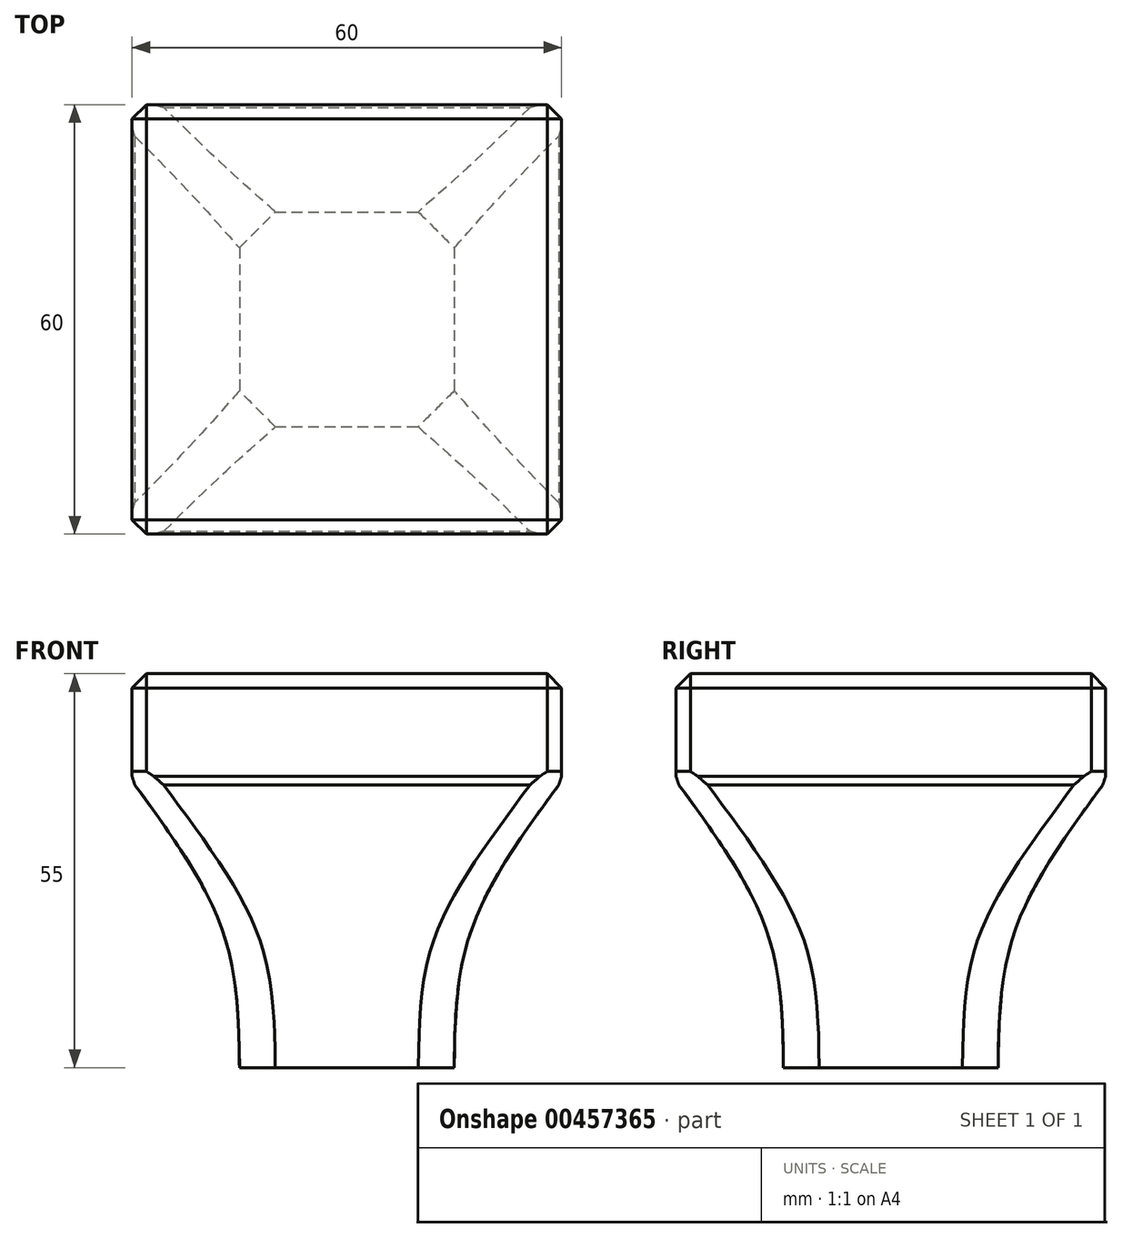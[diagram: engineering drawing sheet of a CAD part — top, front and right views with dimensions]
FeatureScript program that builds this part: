
annotation { "Feature Type Name" : "Feature", "Feature Type Description" : "" }
export const myFeature = defineFeature(function(context is Context, id is Id, definition is map)
    precondition{}
    {
        {
            var Q0;
            Q0=qCreatedBy(makeId("Top.planeOp"),FACE);
            var sketch = newSketch(context, id + "F0", { "sketchPlane" : qUnion([Q0])});
            skLineSegment(sketch, "E0.bottom", {"start": v(30, 30) * mm, "end": v(-30, 30) * mm});
            skLineSegment(sketch, "E0.top", {"start": v(30, -30) * mm, "end": v(-30, -30) * mm});
            skLineSegment(sketch, "E0.left", {"start": v(30, 30) * mm, "end": v(30, -30) * mm});
            skLineSegment(sketch, "E0.right", {"start": v(-30, 30) * mm, "end": v(-30, -30) * mm});
            skPoint(sketch, "E0.middle", {"position": v(0, 0) * mm});
            skSolve(sketch);
        }
        {
            var Q0;
            Q0 = qSketchRegion(id + "F0", true);
            extrude(context, id + "F1", {"entities" : qUnion([Q0]), "depth" : 40 * mm});
        }
        {
            var Q0;
            Q0=makeQuery(id+"F1.opExtrude","SWEPT_FACE",FACE,{"disambiguationData":[OSD([sQuery(id+"F0.wireOp",EDGE,"E0.top")])]});
            var sketch = newSketch(context, id + "F2", { "sketchPlane" : qUnion([Q0])});
            skLineSegment(sketch, "E1", {"start": v(-30, 0) * mm, "end": v(-15, 0) * mm});
            skLineSegment(sketch, "E2", {"start": v(30, 0) * mm, "end": v(15, 0) * mm});
            skLineSegment(sketch, "E3", {"start": v(-30, 40) * mm, "end": v(-30, 0) * mm});
            skLineSegment(sketch, "E4", {"start": v(30, 0) * mm, "end": v(30, 40) * mm});
            skFitSpline(sketch, "E5", {"points": [v(-15, 0) * mm, v(-17.35, 19.1) * mm, v(-30, 40) * mm], "startDerivative": vector(-0.56, 40.9) * mm, "endDerivative": vector(-28.87, 39.13) * mm});
            skFitSpline(sketch, "E6.MirrorCS", {"points": [v(15, 0) * mm, v(17.35, 19.1) * mm, v(30, 40) * mm], "startDerivative": vector(0.56, 40.9) * mm, "endDerivative": vector(28.87, 39.13) * mm});
            skSolve(sketch);
        }
        {
            var Q0;
            Q0=makeQuery(id+"F1.opExtrude","SWEPT_FACE",FACE,{"disambiguationData":[OSD([sQuery(id+"F0.wireOp",EDGE,"E0.left")])]});
            var sketch = newSketch(context, id + "F3", { "sketchPlane" : qUnion([Q0])});
            skLineSegment(sketch, "E7", {"start": v(-30, 0) * mm, "end": v(-15, 0) * mm});
            skLineSegment(sketch, "E8", {"start": v(30, 0) * mm, "end": v(15, 0) * mm});
            skLineSegment(sketch, "E9", {"start": v(-30, 40) * mm, "end": v(-30, 0) * mm});
            skLineSegment(sketch, "E10", {"start": v(30, 0) * mm, "end": v(30, 40) * mm});
            skFitSpline(sketch, "E11", {"points": [v(-15, 0) * mm, v(-17.35, 19.1) * mm, v(-30, 40) * mm], "startDerivative": vector(-0.56, 40.9) * mm, "endDerivative": vector(-28.87, 39.13) * mm});
            skFitSpline(sketch, "E12.MirrorCS", {"points": [v(15, 0) * mm, v(17.35, 19.1) * mm, v(30, 40) * mm], "startDerivative": vector(0.56, 40.9) * mm, "endDerivative": vector(28.87, 39.13) * mm});
            skSolve(sketch);
        }
        {
            var Q0;
            Q0 = qSketchRegion(id + "F2", true);
            extrude(context, id + "F4", {"entities" : qUnion([Q0]), "operationType" : NewBodyOperationType.REMOVE, "oppositeDirection" : true, "depth" : 60 * mm});
        }
        {
            var Q0;
            Q0 = qSketchRegion(id + "F3", true);
            extrude(context, id + "F5", {"entities" : qUnion([Q0]), "operationType" : NewBodyOperationType.REMOVE, "oppositeDirection" : true, "depth" : 60 * mm});
        }
        {
            var Q0;
            Q0=makeQuery(id+"F1.opExtrude","CAP_FACE",FACE,{"disambiguationData":[OSD([sQuery(id+"F0.wireOp",EDGE,"E0.bottom"),sQuery(id+"F0.wireOp",EDGE,"E0.top"),sQuery(id+"F0.wireOp",EDGE,"E0.left"),sQuery(id+"F0.wireOp",EDGE,"E0.right")])],"isStart":false});
            var sketch = newSketch(context, id + "F6", { "sketchPlane" : qUnion([Q0])});
            skLineSegment(sketch, "E13.bottom", {"start": v(30, 30) * mm, "end": v(-30, 30) * mm});
            skLineSegment(sketch, "E13.top", {"start": v(30, -30) * mm, "end": v(-30, -30) * mm});
            skLineSegment(sketch, "E13.left", {"start": v(30, 30) * mm, "end": v(30, -30) * mm});
            skLineSegment(sketch, "E13.right", {"start": v(-30, 30) * mm, "end": v(-30, -30) * mm});
            skPoint(sketch, "E13.middle", {"position": v(0, 0) * mm});
            skSolve(sketch);
        }
        {
            var Q0;
            Q0 = qSketchRegion(id + "F6", true);
            extrude(context, id + "F7", {"entities" : qUnion([Q0]), "operationType" : NewBodyOperationType.ADD, "depth" : 15 * mm});
        }
        {
            var Q0;
            Q0=makeQuery(id+"F5.boolean.opBoolean","INTERSECT",EDGE,{"derivedFrom":[makeQuery(id+"F4.boolean.opBoolean","COPY",FACE,{"derivedFrom":makeQuery(id+"F4.opExtrude","SWEPT_FACE",FACE,{"disambiguationData":[OSD([sQuery(id+"F2.wireOp",EDGE,"E5")])]})}),makeQuery(id+"F5.opExtrude","SWEPT_FACE",FACE,{"disambiguationData":[OSD([sQuery(id+"F3.wireOp",EDGE,"E11")])]})]});
            var Q1;
            Q1=makeQuery(id+"F5.boolean.opBoolean","INTERSECT",EDGE,{"derivedFrom":[makeQuery(id+"F4.boolean.opBoolean","COPY",FACE,{"derivedFrom":makeQuery(id+"F4.opExtrude","SWEPT_FACE",FACE,{"disambiguationData":[OSD([sQuery(id+"F2.wireOp",EDGE,"E6.MirrorCS")])]})}),makeQuery(id+"F5.opExtrude","SWEPT_FACE",FACE,{"disambiguationData":[OSD([sQuery(id+"F3.wireOp",EDGE,"E11")])]})]});
            var Q2;
            Q2=makeQuery(id+"F5.boolean.opBoolean","INTERSECT",EDGE,{"derivedFrom":[makeQuery(id+"F4.boolean.opBoolean","COPY",FACE,{"derivedFrom":makeQuery(id+"F4.opExtrude","SWEPT_FACE",FACE,{"disambiguationData":[OSD([sQuery(id+"F2.wireOp",EDGE,"E6.MirrorCS")])]})}),makeQuery(id+"F5.opExtrude","SWEPT_FACE",FACE,{"disambiguationData":[OSD([sQuery(id+"F3.wireOp",EDGE,"E12.MirrorCS")])]})]});
            var Q3;
            Q3=makeQuery(id+"F5.boolean.opBoolean","INTERSECT",EDGE,{"derivedFrom":[makeQuery(id+"F4.boolean.opBoolean","COPY",FACE,{"derivedFrom":makeQuery(id+"F4.opExtrude","SWEPT_FACE",FACE,{"disambiguationData":[OSD([sQuery(id+"F2.wireOp",EDGE,"E5")])]})}),makeQuery(id+"F5.opExtrude","SWEPT_FACE",FACE,{"disambiguationData":[OSD([sQuery(id+"F3.wireOp",EDGE,"E12.MirrorCS")])]})]});
            chamfer(context, id + "F8", {"entities" : qUnion([Q0, Q1, Q2, Q3]), "width" : 5 * mm, "tangentPropagation" : true});
        }
        {
            var Q0;
            Q0=makeQuery(id+"F7.opExtrude","SWEPT_EDGE",EDGE,{"disambiguationData":[OSD([sQuery(id+"F6.wireOp",EDGE,"E13.top"),sQuery(id+"F6.wireOp",EDGE,"E13.left")])]});
            var Q1;
            Q1=makeQuery(id+"F7.opExtrude","SWEPT_EDGE",EDGE,{"disambiguationData":[OSD([sQuery(id+"F6.wireOp",EDGE,"E13.bottom"),sQuery(id+"F6.wireOp",EDGE,"E13.left")])]});
            var Q2;
            Q2=makeQuery(id+"F7.boolean.opBoolean","MERGE",EDGE,{"derivedFrom":[makeQuery(id+"F4.boolean.opBoolean","MERGE",EDGE,{"derivedFrom":[makeQuery(id+"F1.opExtrude","CAP_EDGE",EDGE,{"disambiguationData":[OSD([sQuery(id+"F0.wireOp",EDGE,"E0.left")])],"isStart":false}),makeQuery(id+"F4.opExtrude","SWEPT_EDGE",EDGE,{"disambiguationData":[OSD([sQuery(id+"F0.wireOp",EDGE,"E0.top"),sQuery(id+"F2.wireOp",EDGE,"E4"),sQuery(id+"F2.wireOp",EDGE,"E6.MirrorCS")])]})]}),makeQuery(id+"F7.opExtrude","CAP_EDGE",EDGE,{"disambiguationData":[OSD([sQuery(id+"F6.wireOp",EDGE,"E13.left")])],"isStart":true})]});
            var Q3;
            Q3=makeQuery(id+"F7.boolean.opBoolean","MERGE",EDGE,{"derivedFrom":[makeQuery(id+"F5.boolean.opBoolean","MERGE",EDGE,{"derivedFrom":[makeQuery(id+"F1.opExtrude","CAP_EDGE",EDGE,{"disambiguationData":[OSD([sQuery(id+"F0.wireOp",EDGE,"E0.bottom")])],"isStart":false}),makeQuery(id+"F5.opExtrude","SWEPT_EDGE",EDGE,{"disambiguationData":[OSD([sQuery(id+"F0.wireOp",EDGE,"E0.left"),sQuery(id+"F3.wireOp",EDGE,"E10"),sQuery(id+"F3.wireOp",EDGE,"E12.MirrorCS")])]})]}),makeQuery(id+"F7.opExtrude","CAP_EDGE",EDGE,{"disambiguationData":[OSD([sQuery(id+"F6.wireOp",EDGE,"E13.bottom")])],"isStart":true})]});
            var Q4;
            Q4=makeQuery(id+"F7.opExtrude","SWEPT_EDGE",EDGE,{"disambiguationData":[OSD([sQuery(id+"F6.wireOp",EDGE,"E13.bottom"),sQuery(id+"F6.wireOp",EDGE,"E13.right")])]});
            var Q5;
            Q5=makeQuery(id+"F7.boolean.opBoolean","MERGE",EDGE,{"derivedFrom":[makeQuery(id+"F4.boolean.opBoolean","MERGE",EDGE,{"derivedFrom":[makeQuery(id+"F1.opExtrude","CAP_EDGE",EDGE,{"disambiguationData":[OSD([sQuery(id+"F0.wireOp",EDGE,"E0.right")])],"isStart":false}),makeQuery(id+"F4.opExtrude","SWEPT_EDGE",EDGE,{"disambiguationData":[OSD([sQuery(id+"F0.wireOp",EDGE,"E0.top"),sQuery(id+"F2.wireOp",EDGE,"E3"),sQuery(id+"F2.wireOp",EDGE,"E5")])]})]}),makeQuery(id+"F7.opExtrude","CAP_EDGE",EDGE,{"disambiguationData":[OSD([sQuery(id+"F6.wireOp",EDGE,"E13.right")])],"isStart":true})]});
            var Q6;
            Q6=makeQuery(id+"F7.opExtrude","SWEPT_EDGE",EDGE,{"disambiguationData":[OSD([sQuery(id+"F6.wireOp",EDGE,"E13.top"),sQuery(id+"F6.wireOp",EDGE,"E13.right")])]});
            var Q7;
            Q7=makeQuery(id+"F7.boolean.opBoolean","MERGE",EDGE,{"derivedFrom":[makeQuery(id+"F5.boolean.opBoolean","MERGE",EDGE,{"derivedFrom":[makeQuery(id+"F1.opExtrude","CAP_EDGE",EDGE,{"disambiguationData":[OSD([sQuery(id+"F0.wireOp",EDGE,"E0.top")])],"isStart":false}),makeQuery(id+"F5.opExtrude","SWEPT_EDGE",EDGE,{"disambiguationData":[OSD([sQuery(id+"F0.wireOp",EDGE,"E0.left"),sQuery(id+"F3.wireOp",EDGE,"E9"),sQuery(id+"F3.wireOp",EDGE,"E11")])]})]}),makeQuery(id+"F7.opExtrude","CAP_EDGE",EDGE,{"disambiguationData":[OSD([sQuery(id+"F6.wireOp",EDGE,"E13.top")])],"isStart":true})]});
            var Q8;
            Q8=makeQuery(id+"F7.opExtrude","CAP_EDGE",EDGE,{"disambiguationData":[OSD([sQuery(id+"F6.wireOp",EDGE,"E13.top")])],"isStart":false});
            var Q9;
            Q9=makeQuery(id+"F7.opExtrude","CAP_EDGE",EDGE,{"disambiguationData":[OSD([sQuery(id+"F6.wireOp",EDGE,"E13.right")])],"isStart":false});
            var Q10;
            Q10=makeQuery(id+"F7.opExtrude","CAP_EDGE",EDGE,{"disambiguationData":[OSD([sQuery(id+"F6.wireOp",EDGE,"E13.bottom")])],"isStart":false});
            var Q11;
            Q11=makeQuery(id+"F7.opExtrude","CAP_EDGE",EDGE,{"disambiguationData":[OSD([sQuery(id+"F6.wireOp",EDGE,"E13.left")])],"isStart":false});
            chamfer(context, id + "F9", {"entities" : qUnion([Q0, Q1, Q2, Q3, Q4, Q5, Q6, Q7, Q8, Q9, Q10, Q11]), "width" : 2 * mm, "tangentPropagation" : true});
        }
    });
